FCSTD DOCUMENT  (FreeCAD 1.0R39109 (Git))
Label: Master Document
License: All rights reserved
LicenseURL: http://en.wikipedia.org/wiki/All_rights_reserved
objects: Spreadsheet::Sheet×1

FEATURE [Spreadsheet::Sheet] Spreadsheet  label="Monitor Chassis Parameters"
  cells = A1='Parameter Name; B1='Value; C1='Notes; A2='GSWallWidth; B2(GSWallWidth)=123; A3='GSBaseFloorBeamWidth; B3(GSBaseFloorBeamWidth)==B30 * 3; C3='Is relelative to the size of the screw hole size; A4='GSBaseBodyThickness; B4(GSBaseBodyThickness)=3; A5='GSCamWallThickness; B5(GSCamWallThickness)=4; A6='GSThinWallThickness; B6(GSThinWallThickness)=3; A7='GSCamWallClickIndent; B7(GSCamWallClickIndent)=1; A8='GSCamWallClickLength; B8(GSCamWallClickLength)=6; A9='GSCamWallFullClickStructureHeight; B9(GSCamWallFullClickStructureHeight)=20; A12='GSCamBoardHeight; B12(GSCamBoardHeight)=38; A13='GSCamBoardWidth; B13(GSCamBoardWidth)=38; A14='GSCamBoardMountingHoleDiameter; B14(GSCamBoardMountingHoleDiameter)==B39; A15='GSCamPlateThickness; B15(GSCamPlateThickness)=4; A16='GSCamMountingHoleOffset; B16(GSCamMountingHoleOffset)=4; A17='GSCamMountingHoleThickness; B17(GSCamMountingHoleThickness)=2; A18='GSCamMountingHoleHeight; B18(GSCamMountingHoleHeight)=7; A19='GSCamAxisHoleDiameter; B19(GSCamAxisHoleDiameter)==B40; C19='M4 uses a 4.5 mm hole; A20='GSCamAxisWidth; B20(GSCamAxisWidth)=22; A21='GSCamMountingHoleDiameter; B21(GSCamMountingHoleDiameter)=2.5; A22='GSCamGimbalDepth; B22(GSCamGimbalDepth)=20; A23='GSCam1ZAxisSetback; B23(GSCam1ZAxisSetback)=25; C23='The camera will be mounted back, away from the lens to help the tilt ability; A24='GSCam2ZAxisSetback; B24(GSCam2ZAxisSetback)=25; C24='The camera will be mounted back, away from the lens to help the tilt ability; A25='GSCamGimbalLighteningSlotOffsetFromCenter; B25(GSCamGimbalLighteningSlotOffsetFromCenter)=12; A26='GSCamGimbalInnerLength; B26(GSCamGimbalInnerLength)=58; A27='GSCam1GimbalHoleHeight; B27(GSCam1GimbalHoleHeight)=50; A28='GSCam2GimbalHoleHeight; B28(GSCam2GimbalHoleHeight)=35; A29='GSCamM4NutHexagonDiameter; B29(GSCamM4NutHexagonDiameter)=8.4; A30='GSCamM4ScrewHoleDiameter; B30(GSCamM4ScrewHoleDiameter)=3.3; A31='GSCamM4NutDepth; B31(GSCamM4SNutDepth)=4; A32='GSCamM3NutDepth; B32(GSCamM3NutDepth)=3.5; A33='GSCamM5NutHexagonDiameter; B33(GSCamM5NutHexagonDiameter)=9.5; A34='GSCamM3NutHexagonDiameter; B34(GSCamM3NutHexagonDiameter)=6.6; A35='GSCamM5ScrewHoleDiameter; B35(GSCamM5ScrewHoleDiameter)=5.5; A36='GSCamM5NutDepth; B36(GSCamM5NutDepth)=4; A37='GSLEDPowerRiserHeight; B37(GSLEDPowerRiserHeight)=7; A38='GSM3BoltHoleDiameter; B38(GSM3BoltHoleDiameter)=3.4; A39='GSM25BoltHoleDiameter; B39(GSM25BoltHoleDiameter)=2.9; A40='GSM4BoltHoleDiameter; B40(GSM4BoltHoleDiameter)=4.5; A41='GSM4BoltHeadIndentDiameter; B41(GSM4BoltHeadIndentDiameter)=7.5; A42='GSM3TappingScrewHoleDiameter; B42(GSM3TappingScrewHoleDiameter)=2.4; A43='GSM5ScrewHoleDiameter; B43(GSM5ScrewHoleDiameter)=3.3; A45='GSLEDBackplateCoolingSlotLength; B45(GSLEDBackplateCoolingSlotLength)=25; A46='GSLEDBackplateCoolingSlotWidth; B46(GSLEDBackplateCoolingSlotWidth)=5; A47='GSLEDMountingRiserHeight; B47(GSLEDMountingRiserHeight)=8; A48='GSLEDMountingHoleSeparation; B48(GSLEDMountingHoleSeparation)=34; A49='GSCamGimbalHoleHeight; B49(GSCamGimbalHoleHeight)=41; A50='GSLEDBoardWingThickness; B50(GSLEDBoardWingThickness)=2; A51='GSLEDBoardHeight; B51(GSLEDBoardHeight)=60; A52='GSLEDBoardWidth; B52(GSLEDBoardWidth)=60; A53='GSLEDZAxisSetback; B53(GSLEDZAxisSetback)=15; A54='GSLEDMountHoleDiameter; B54(GSLEDMountHoleDiameter)=2.5; A55='GSLEDMountingRiserOuterDiameter; B55(GSLEDMountingRiserOuterDiameter)=7; A56='GSLEDLensMountingRiserHeight; B56(GSLEDLensMountingRiserHeight)=15; A57='GSLEDLensMountingHoleSeparation; B57(GSLEDLensMountingHoleSeparation)=47; A58='GSLEDLensMountingRiserOuterDiameter; B58(GSLEDLensMountingRiserOuterDiameter)=7; A59='GSLEDLensMountingScrewHoleDiameter; B59(GSLEDLensMountingScrewHoleDiameter)=2.5; A60='GSLEDGimbalHoleHeight; B60(GSLEDGimbalHoleHeight)=40; A61='GSLEDGimbalBaseLength; B61(GSLEDGimbalBaseLength)==GSLEDBoardWidth + 2 * (GSLEDBoardWingThickness + GSCamPlateThickness * 2)
